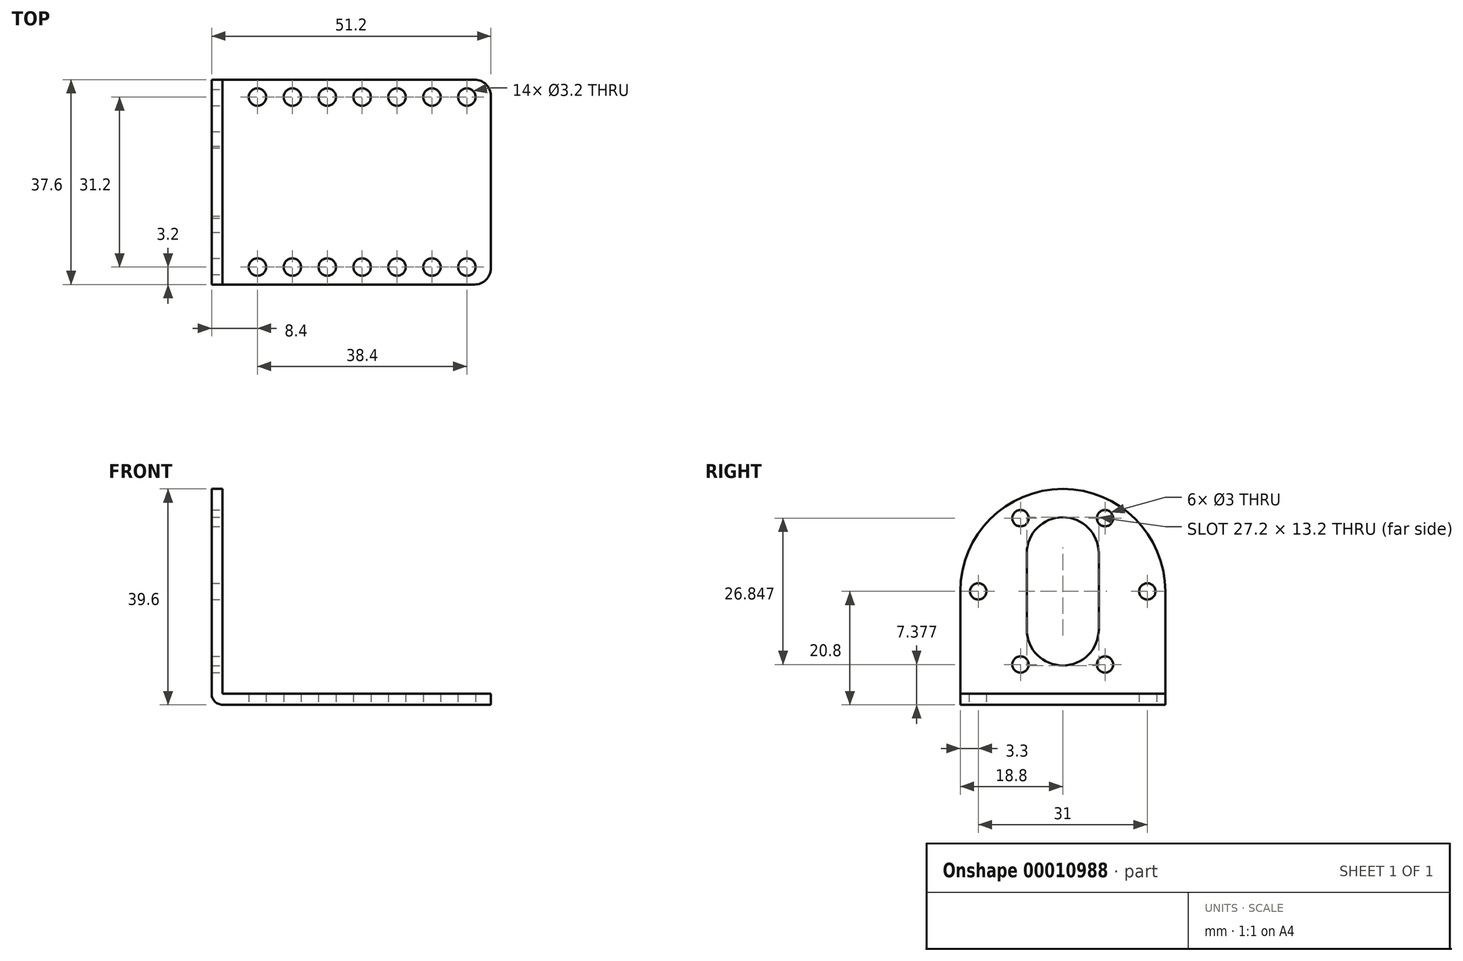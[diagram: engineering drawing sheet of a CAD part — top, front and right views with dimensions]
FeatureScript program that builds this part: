
annotation { "Feature Type Name" : "Feature", "Feature Type Description" : "" }
export const myFeature = defineFeature(function(context is Context, id is Id, definition is map)
    precondition{}
    {
        {
            var Q0;
            Q0=qCreatedBy(makeId("Top.planeOp"),FACE);
            var sketch = newSketch(context, id + "F0", { "sketchPlane" : qUnion([Q0])});
            skLineSegment(sketch, "E0.bottom", {"start": v(0, 0) * mm, "end": v(46.2, 0) * mm});
            skLineSegment(sketch, "E0.top", {"start": v(0, -37.6) * mm, "end": v(46.2, -37.6) * mm});
            skLineSegment(sketch, "E0.left", {"start": v(0, 0) * mm, "end": v(0, -37.6) * mm});
            skLineSegment(sketch, "E0.right", {"start": v(49.2, -3) * mm, "end": v(49.2, -34.6) * mm});
            skCircle(sketch, "E1", {"center": v(6.4, -3.2) * mm, "radius": 1.6 * mm});
            skCircle(sketch, "E2.0.1.0", {"center": v(6.4, -34.4) * mm, "radius": 1.6 * mm});
            skCircle(sketch, "E2.1.0.0", {"center": v(12.8, -3.2) * mm, "radius": 1.6 * mm});
            skCircle(sketch, "E2.1.1.0", {"center": v(12.8, -34.4) * mm, "radius": 1.6 * mm});
            skCircle(sketch, "E2.2.0.0", {"center": v(19.2, -3.2) * mm, "radius": 1.6 * mm});
            skCircle(sketch, "E2.2.1.0", {"center": v(19.2, -34.4) * mm, "radius": 1.6 * mm});
            skCircle(sketch, "E2.3.0.0", {"center": v(25.6, -3.2) * mm, "radius": 1.6 * mm});
            skCircle(sketch, "E2.3.1.0", {"center": v(25.6, -34.4) * mm, "radius": 1.6 * mm});
            skCircle(sketch, "E2.4.0.0", {"center": v(32, -3.2) * mm, "radius": 1.6 * mm});
            skCircle(sketch, "E2.4.1.0", {"center": v(32, -34.4) * mm, "radius": 1.6 * mm});
            skCircle(sketch, "E2.5.0.0", {"center": v(38.4, -3.2) * mm, "radius": 1.6 * mm});
            skCircle(sketch, "E2.5.1.0", {"center": v(38.4, -34.4) * mm, "radius": 1.6 * mm});
            skCircle(sketch, "E2.6.0.0", {"center": v(44.8, -3.2) * mm, "radius": 1.6 * mm});
            skCircle(sketch, "E2.6.1.0", {"center": v(44.8, -34.4) * mm, "radius": 1.6 * mm});
            skLineSegment(sketch, "E2.direction1", {"start": v(6.4, -3.2) * mm, "end": v(12.8, -3.2) * mm, "construction": true});
            skLineSegment(sketch, "E2.direction2", {"start": v(6.4, -3.2) * mm, "end": v(6.4, -34.4) * mm, "construction": true});
            skPoint(sketch, "E3.visualSharp", {"position": v(49.2, 0) * mm});
            skArc(sketch, "E3.filletArc", {"start": v(49.2, -3) * mm, "mid": v(48.32, -0.88) * mm, "end": v(46.2, 0) * mm});
            skPoint(sketch, "E4.visualSharp", {"position": v(49.2, -37.6) * mm});
            skArc(sketch, "E4.filletArc", {"start": v(46.2, -37.6) * mm, "mid": v(48.32, -36.72) * mm, "end": v(49.2, -34.6) * mm});
            skSolve(sketch);
        }
        {
            var Q0;
            Q0=qCreatedBy(makeId("Right.planeOp"),FACE);
            var sketch = newSketch(context, id + "F1", { "sketchPlane" : qUnion([Q0])});
            skLineSegment(sketch, "E5", {"start": v(0, 0) * mm, "end": v(0, 20.8) * mm});
            skLineSegment(sketch, "E6", {"start": v(-37.6, 0) * mm, "end": v(-37.6, 20.8) * mm});
            skArc(sketch, "E7", {"start": v(0, 20.8) * mm, "mid": v(-18.8, 39.6) * mm, "end": v(-37.6, 20.8) * mm});
            skLineSegment(sketch, "E8", {"start": v(0, 0) * mm, "end": v(-37.6, 0) * mm});
            skCircle(sketch, "E9", {"center": v(-3.3, 20.8) * mm, "radius": 1.5 * mm});
            skCircle(sketch, "E10.1.0", {"center": v(-11.05, 34.22) * mm, "radius": 1.5 * mm});
            skCircle(sketch, "E10.2.0", {"center": v(-26.55, 34.22) * mm, "radius": 1.5 * mm});
            skCircle(sketch, "E10.3.0", {"center": v(-34.3, 20.8) * mm, "radius": 1.5 * mm});
            skCircle(sketch, "E10.4.0", {"center": v(-26.55, 7.38) * mm, "radius": 1.5 * mm});
            skCircle(sketch, "E10.5.0", {"center": v(-11.05, 7.38) * mm, "radius": 1.5 * mm});
            skLineSegment(sketch, "E11.rect.bottom", {"start": v(-25.4, 13.8) * mm, "end": v(-12.2, 13.8) * mm});
            skLineSegment(sketch, "E11.rect.top", {"start": v(-25.4, 27.8) * mm, "end": v(-12.2, 27.8) * mm});
            skLineSegment(sketch, "E11.rect.left", {"start": v(-25.4, 13.8) * mm, "end": v(-25.4, 27.8) * mm});
            skLineSegment(sketch, "E11.rect.right", {"start": v(-12.2, 13.8) * mm, "end": v(-12.2, 27.8) * mm});
            skArc(sketch, "E12", {"start": v(-12.2, 27.8) * mm, "mid": v(-18.8, 34.4) * mm, "end": v(-25.4, 27.8) * mm});
            skArc(sketch, "E13", {"start": v(-25.4, 13.8) * mm, "mid": v(-18.8, 7.2) * mm, "end": v(-12.2, 13.8) * mm});
            skSolve(sketch);
        }
        {
            var Q0;
            Q0=makeQuery(id+"F0.imprint","IMPRINT",FACE,{"disambiguationData":[TD([[makeQuery(id+"F0.imprint","IMPRINT",EDGE,{"derivedFrom":sQuery(id+"F0.wireOp",EDGE,"E0.bottom")}),-1.0]])]});
            extrude(context, id + "F2", {"entities" : qUnion([Q0]), "depth" : 2 * mm});
        }
        {
            var Q0;
            Q0=makeQuery(id+"F1.imprint","IMPRINT",FACE,{"disambiguationData":[TD([[makeQuery(id+"F1.imprint","IMPRINT",EDGE,{"derivedFrom":sQuery(id+"F1.wireOp",EDGE,"E5")}),1.0]])]});
            extrude(context, id + "F3", {"entities" : qUnion([Q0]), "operationType" : NewBodyOperationType.ADD, "oppositeDirection" : true, "depth" : 2 * mm});
        }
        {
            var Q0;
            Q0=makeQuery(id+"F3.opExtrude","CAP_EDGE",EDGE,{"disambiguationData":[OSD([sQuery(id+"F1.wireOp",EDGE,"E8")])],"isStart":false});
            fillet(context, id + "F4", {"entities" : qUnion([Q0]), "radius" : 2 * mm, "tangentPropagation" : true, "allowEdgeOverflow" : false});
        }
    });
